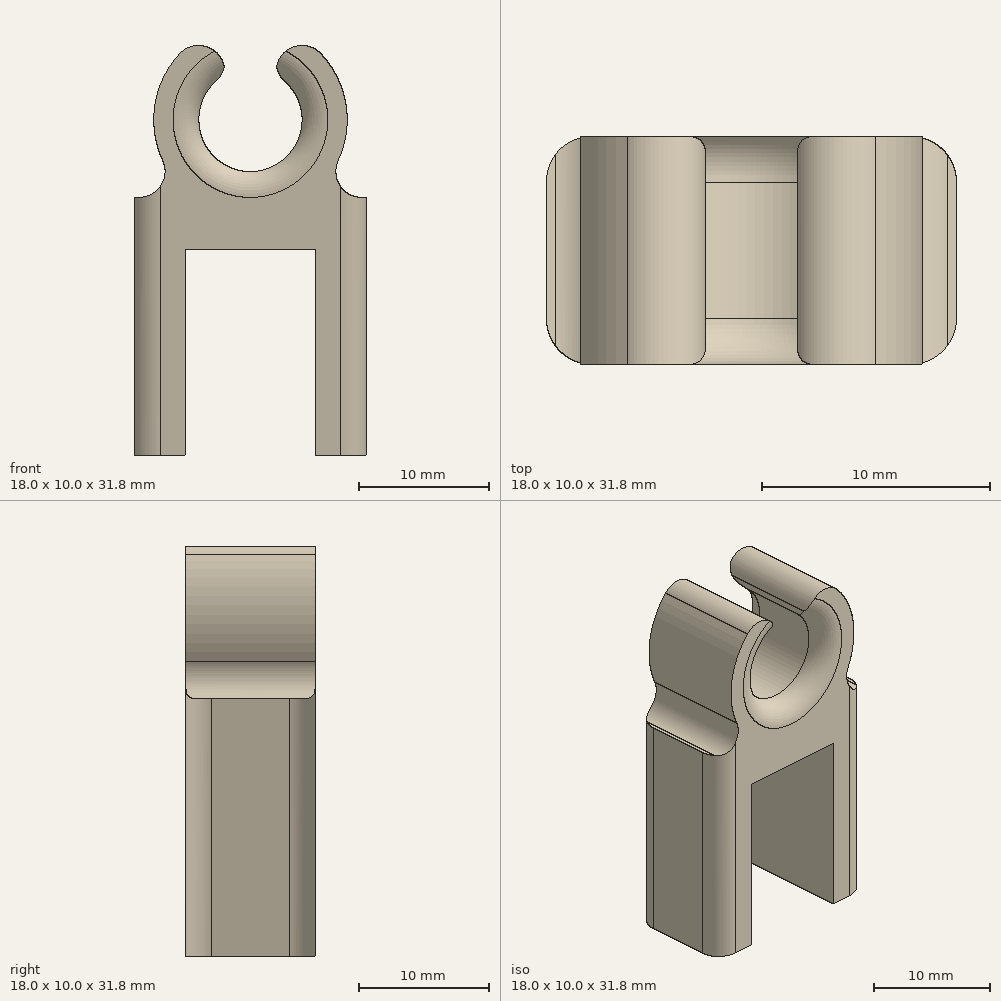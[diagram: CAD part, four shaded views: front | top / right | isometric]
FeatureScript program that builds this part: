
annotation { "Feature Type Name" : "Feature", "Feature Type Description" : "" }
export const myFeature = defineFeature(function(context is Context, id is Id, definition is map)
    precondition{}
    {
        {
            var Q0;
            Q0=qCreatedBy(makeId("Front.planeOp"),FACE);
            var sketch = newSketch(context, id + "F0", { "sketchPlane" : qUnion([Q0])});
            skLineSegment(sketch, "E0", {"start": v(0, 0) * mm, "end": v(0, 16) * mm});
            skLineSegment(sketch, "E1", {"start": v(0, 16) * mm, "end": v(10, 16) * mm});
            skLineSegment(sketch, "E2", {"start": v(10, 16) * mm, "end": v(10, 0) * mm});
            skLineSegment(sketch, "E3", {"start": v(0, 0) * mm, "end": v(-4, 0) * mm});
            skLineSegment(sketch, "E4", {"start": v(10, 0) * mm, "end": v(14, 0) * mm});
            skLineSegment(sketch, "E5.0", {"start": v(14, 20) * mm, "end": v(14, 0) * mm});
            skLineSegment(sketch, "E5.1", {"start": v(-4, 20) * mm, "end": v(14, 20) * mm});
            skLineSegment(sketch, "E5.2", {"start": v(-4, 0) * mm, "end": v(-4, 20) * mm});
            skSolve(sketch);
        }
        {
            var Q0;
            Q0 = qSketchRegion(id + "F0", true);
            extrude(context, id + "F1", {"entities" : qUnion([Q0]), "endBound" : BoundingType.SYMMETRIC, "depth" : 10 * mm, "offsetDistance" : 25 * mm});
        }
        {
            var Q0;
            Q0=qCreatedBy(makeId("Front.planeOp"),FACE);
            var sketch = newSketch(context, id + "F2", { "sketchPlane" : qUnion([Q0])});
            skCircle(sketch, "E6", {"center": v(5, 26) * mm, "radius": 7.5 * mm});
            skCircle(sketch, "E7", {"center": v(5, 26) * mm, "radius": 4 * mm});
            skSolve(sketch);
        }
        {
            var Q0;
            Q0 = qSketchRegion(id + "F2", true);
            extrude(context, id + "F3", {"entities" : qUnion([Q0]), "operationType" : NewBodyOperationType.ADD, "endBound" : BoundingType.SYMMETRIC, "depth" : 10 * mm, "offsetDistance" : 25 * mm});
        }
        {
            var Q0;
            Q0=qCreatedBy(makeId("Front.planeOp"),FACE);
            var sketch = newSketch(context, id + "F4", { "sketchPlane" : qUnion([Q0])});
            skLineSegment(sketch, "E8.bottom", {"start": v(7, 26.84) * mm, "end": v(3, 26.84) * mm});
            skLineSegment(sketch, "E8.top", {"start": v(7, 36.84) * mm, "end": v(3, 36.84) * mm});
            skLineSegment(sketch, "E8.left", {"start": v(7, 26.84) * mm, "end": v(7, 36.84) * mm});
            skLineSegment(sketch, "E8.right", {"start": v(3, 26.84) * mm, "end": v(3, 36.84) * mm});
            skPoint(sketch, "E8.middle", {"position": v(5, 31.84) * mm});
            skSolve(sketch);
        }
        {
            var Q0;
            Q0 = qSketchRegion(id + "F4", true);
            extrude(context, id + "F5", {"entities" : qUnion([Q0]), "operationType" : NewBodyOperationType.REMOVE, "endBound" : BoundingType.SYMMETRIC, "oppositeDirection" : true, "depth" : 11.4 * mm, "offsetDistance" : 25 * mm});
        }
        {
            var Q0;
            Q0=makeQuery(id+"F3.boolean.opBoolean","INTERSECT",EDGE,{"disambiguationData":[OD(1.0)],"derivedFrom":[makeQuery(id+"F1.opExtrude","SWEPT_FACE",FACE,{"disambiguationData":[OSD([sQuery(id+"F0.wireOp",EDGE,"E5.1")])]}),makeQuery(id+"F3.opExtrude","SWEPT_FACE",FACE,{"disambiguationData":[OSD([sQuery(id+"F2.wireOp",EDGE,"E6")])]})]});
            var Q1;
            Q1=makeQuery(id+"F3.boolean.opBoolean","INTERSECT",EDGE,{"disambiguationData":[OD(0.0)],"derivedFrom":[makeQuery(id+"F1.opExtrude","SWEPT_FACE",FACE,{"disambiguationData":[OSD([sQuery(id+"F0.wireOp",EDGE,"E5.1")])]}),makeQuery(id+"F3.opExtrude","SWEPT_FACE",FACE,{"disambiguationData":[OSD([sQuery(id+"F2.wireOp",EDGE,"E6")])]})]});
            var Q2;
            Q2=makeQuery(id+"F5.boolean.opBoolean","INTERSECT",EDGE,{"derivedFrom":[makeQuery(id+"F3.opExtrude","SWEPT_FACE",FACE,{"disambiguationData":[OSD([sQuery(id+"F2.wireOp",EDGE,"E6")])]}),makeQuery(id+"F5.opExtrude","SWEPT_FACE",FACE,{"disambiguationData":[OSD([sQuery(id+"F4.wireOp",EDGE,"E8.left")])]})]});
            var Q3;
            Q3=makeQuery(id+"F5.boolean.opBoolean","INTERSECT",EDGE,{"derivedFrom":[makeQuery(id+"F3.opExtrude","SWEPT_FACE",FACE,{"disambiguationData":[OSD([sQuery(id+"F2.wireOp",EDGE,"E7")])]}),makeQuery(id+"F5.opExtrude","SWEPT_FACE",FACE,{"disambiguationData":[OSD([sQuery(id+"F4.wireOp",EDGE,"E8.left")])]})]});
            var Q4;
            Q4=makeQuery(id+"F5.boolean.opBoolean","INTERSECT",EDGE,{"derivedFrom":[makeQuery(id+"F3.opExtrude","SWEPT_FACE",FACE,{"disambiguationData":[OSD([sQuery(id+"F2.wireOp",EDGE,"E7")])]}),makeQuery(id+"F5.opExtrude","SWEPT_FACE",FACE,{"disambiguationData":[OSD([sQuery(id+"F4.wireOp",EDGE,"E8.right")])]})]});
            var Q5;
            Q5=makeQuery(id+"F5.boolean.opBoolean","INTERSECT",EDGE,{"derivedFrom":[makeQuery(id+"F3.opExtrude","SWEPT_FACE",FACE,{"disambiguationData":[OSD([sQuery(id+"F2.wireOp",EDGE,"E6")])]}),makeQuery(id+"F5.opExtrude","SWEPT_FACE",FACE,{"disambiguationData":[OSD([sQuery(id+"F4.wireOp",EDGE,"E8.right")])]})]});
            fillet(context, id + "F6", {"entities" : qUnion([Q0, Q1, Q2, Q3, Q4, Q5]), "radius" : 2 * mm, "tangentPropagation" : true, "allowEdgeOverflow" : false});
        }
        {
            var Q0;
            Q0=makeQuery(id+"F1.opExtrude","CAP_EDGE",EDGE,{"disambiguationData":[OSD([sQuery(id+"F0.wireOp",EDGE,"E5.2")])],"isStart":false});
            var Q1;
            Q1=makeQuery(id+"F1.opExtrude","CAP_EDGE",EDGE,{"disambiguationData":[OSD([sQuery(id+"F0.wireOp",EDGE,"E5.0")])],"isStart":false});
            var Q2;
            Q2=makeQuery(id+"F1.opExtrude","CAP_EDGE",EDGE,{"disambiguationData":[OSD([sQuery(id+"F0.wireOp",EDGE,"E5.0")])],"isStart":true});
            var Q3;
            Q3=makeQuery(id+"F1.opExtrude","CAP_EDGE",EDGE,{"disambiguationData":[OSD([sQuery(id+"F0.wireOp",EDGE,"E5.2")])],"isStart":true});
            fillet(context, id + "F7", {"entities" : qUnion([Q0, Q1, Q2, Q3]), "radius" : 2 * mm, "tangentPropagation" : true, "allowEdgeOverflow" : false});
        }
        {
            var Q0;
            Q0=makeQuery(id+"F3.opExtrude","CAP_EDGE",EDGE,{"disambiguationData":[OSD([sQuery(id+"F2.wireOp",EDGE,"E7")])],"isStart":false});
            var Q1;
            Q1=makeQuery(id+"F3.opExtrude","CAP_EDGE",EDGE,{"disambiguationData":[OSD([sQuery(id+"F2.wireOp",EDGE,"E7")])],"isStart":true});
            fillet(context, id + "F8", {"entities" : qUnion([Q0, Q1]), "radius" : 2 * mm, "tangentPropagation" : true, "allowEdgeOverflow" : false});
        }
    });
